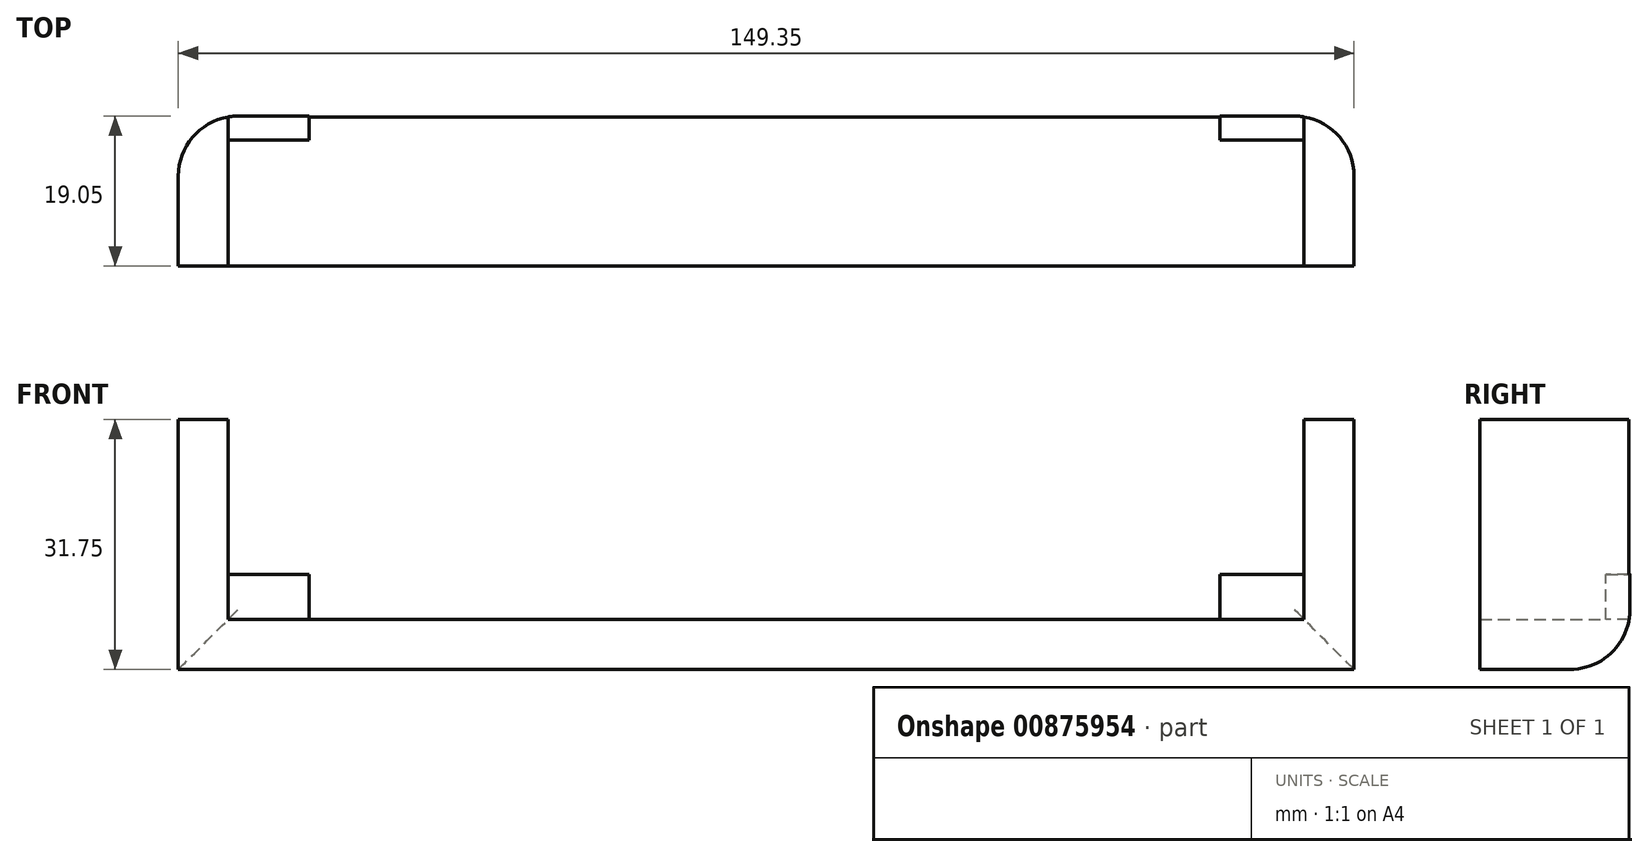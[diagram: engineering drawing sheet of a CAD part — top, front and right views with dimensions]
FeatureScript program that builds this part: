
annotation { "Feature Type Name" : "Feature", "Feature Type Description" : "" }
export const myFeature = defineFeature(function(context is Context, id is Id, definition is map)
    precondition{}
    {
        {
            var Q0;
            Q0=qCreatedBy(makeId("Front.planeOp"),FACE);
            var sketch = newSketch(context, id + "F0", { "sketchPlane" : qUnion([Q0])});
            skLineSegment(sketch, "E0", {"start": v(-38.09, 19.67) * mm, "end": v(-38.09, -5.73) * mm});
            skLineSegment(sketch, "E1", {"start": v(-38.09, -5.73) * mm, "end": v(98.56, -5.73) * mm});
            skLineSegment(sketch, "E2", {"start": v(98.56, -5.73) * mm, "end": v(98.56, 19.67) * mm});
            skLineSegment(sketch, "E3.0", {"start": v(104.91, -12.08) * mm, "end": v(104.91, 19.67) * mm});
            skLineSegment(sketch, "E3.1", {"start": v(-44.44, -12.08) * mm, "end": v(104.91, -12.08) * mm});
            skLineSegment(sketch, "E3.2", {"start": v(-44.44, 19.67) * mm, "end": v(-44.44, -12.08) * mm});
            skLineSegment(sketch, "E4", {"start": v(-44.44, 19.67) * mm, "end": v(-38.09, 19.67) * mm});
            skLineSegment(sketch, "E5", {"start": v(98.56, 19.67) * mm, "end": v(104.91, 19.67) * mm});
            skSolve(sketch);
        }
        {
            var Q0;
            Q0 = qSketchRegion(id + "F0", true);
            extrude(context, id + "F1", {"entities" : qUnion([Q0]), "depth" : 19.05 * mm, "offsetDistance" : 25.4 * mm});
        }
        {
            var Q0;
            Q0=qCreatedBy(makeId("Front.planeOp"),FACE);
            var sketch = newSketch(context, id + "F2", { "sketchPlane" : qUnion([Q0])});
            skLineSegment(sketch, "E6.bottom", {"start": v(-38.09, 0) * mm, "end": v(-27.8, 0) * mm});
            skLineSegment(sketch, "E6.top", {"start": v(-38.09, -5.97) * mm, "end": v(-27.8, -5.97) * mm});
            skLineSegment(sketch, "E6.left", {"start": v(-38.09, 0) * mm, "end": v(-38.09, -5.97) * mm});
            skLineSegment(sketch, "E6.right", {"start": v(-27.8, 0) * mm, "end": v(-27.8, -5.97) * mm});
            skLineSegment(sketch, "E7.bottom", {"start": v(98.67, -5.97) * mm, "end": v(87.9, -5.97) * mm});
            skLineSegment(sketch, "E7.top", {"start": v(98.67, 0) * mm, "end": v(87.9, 0) * mm});
            skLineSegment(sketch, "E7.left", {"start": v(98.67, -5.97) * mm, "end": v(98.67, 0) * mm});
            skLineSegment(sketch, "E7.right", {"start": v(87.9, -5.97) * mm, "end": v(87.9, 0) * mm});
            skSolve(sketch);
        }
        {
            var Q0;
            Q0 = qSketchRegion(id + "F2", true);
            extrude(context, id + "F3", {"entities" : qUnion([Q0]), "operationType" : NewBodyOperationType.ADD, "depth" : 3.05 * mm, "offsetDistance" : 25.4 * mm});
        }
        {
            var Q0;
            Q0=makeQuery(id+"F1.opExtrude","CAP_EDGE",EDGE,{"disambiguationData":[OSD([sQuery(id+"F0.wireOp",EDGE,"E3.0")])],"isStart":true});
            var Q1;
            Q1=makeQuery(id+"F1.opExtrude","CAP_EDGE",EDGE,{"disambiguationData":[OSD([sQuery(id+"F0.wireOp",EDGE,"E3.1")])],"isStart":true});
            var Q2;
            Q2=makeQuery(id+"F1.opExtrude","CAP_EDGE",EDGE,{"disambiguationData":[OSD([sQuery(id+"F0.wireOp",EDGE,"E3.2")])],"isStart":true});
            fillet(context, id + "F4", {"entities" : qUnion([Q0, Q1, Q2]), "radius" : 7.62 * mm, "tangentPropagation" : true, "allowEdgeOverflow" : false});
        }
    });
